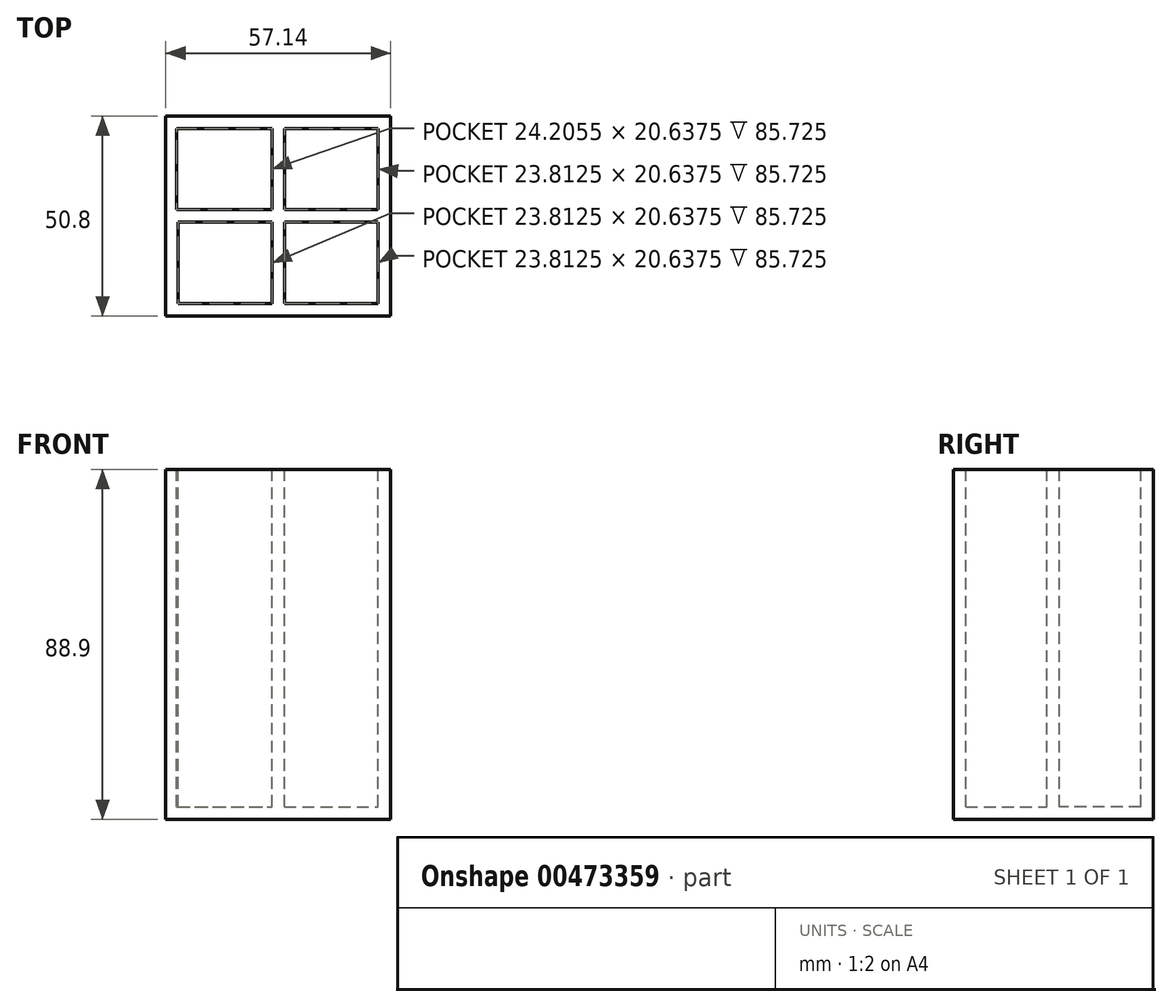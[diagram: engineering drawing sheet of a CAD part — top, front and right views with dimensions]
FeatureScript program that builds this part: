
annotation { "Feature Type Name" : "Feature", "Feature Type Description" : "" }
export const myFeature = defineFeature(function(context is Context, id is Id, definition is map)
    precondition{}
    {
        {
            var Q0;
            Q0=qCreatedBy(makeId("Front.planeOp"),FACE);
            var sketch = newSketch(context, id + "F0", { "sketchPlane" : qUnion([Q0])});
            skLineSegment(sketch, "E0.bottom", {"start": v(-28.57, 44.45) * mm, "end": v(28.58, 44.45) * mm});
            skLineSegment(sketch, "E0.top", {"start": v(-28.58, -44.45) * mm, "end": v(28.58, -44.45) * mm});
            skLineSegment(sketch, "E0.left", {"start": v(-28.57, 44.45) * mm, "end": v(-28.58, -44.45) * mm});
            skLineSegment(sketch, "E0.right", {"start": v(28.58, 44.45) * mm, "end": v(28.58, -44.45) * mm});
            skPoint(sketch, "E0.middle", {"position": v(0, 0) * mm});
            skSolve(sketch);
        }
        {
            var Q0;
            Q0 = qSketchRegion(id + "F0", true);
            extrude(context, id + "F1", {"entities" : qUnion([Q0]), "depth" : 50.8 * mm});
        }
        {
            var Q0;
            Q0=makeQuery(id+"F1.opExtrude","SWEPT_FACE",FACE,{"disambiguationData":[OSD([sQuery(id+"F0.wireOp",EDGE,"E0.bottom")])]});
            var sketch = newSketch(context, id + "F2", { "sketchPlane" : qUnion([Q0])});
            skLineSegment(sketch, "E1.bottom", {"start": v(-25.8, -3.18) * mm, "end": v(-1.59, -3.18) * mm});
            skLineSegment(sketch, "E1.top", {"start": v(-25.8, -23.81) * mm, "end": v(-1.59, -23.81) * mm});
            skLineSegment(sketch, "E1.left", {"start": v(-25.8, -3.18) * mm, "end": v(-25.8, -23.81) * mm});
            skLineSegment(sketch, "E1.right", {"start": v(-1.59, -3.17) * mm, "end": v(-1.59, -23.81) * mm});
            skSolve(sketch);
        }
        {
            var Q0;
            Q0 = qSketchRegion(id + "F2", true);
            extrude(context, id + "F3", {"entities" : qUnion([Q0]), "operationType" : NewBodyOperationType.REMOVE, "oppositeDirection" : true, "depth" : 85.72 * mm});
        }
        {
            var Q0;
            Q0=makeQuery(id+"F1.opExtrude","SWEPT_FACE",FACE,{"disambiguationData":[OSD([sQuery(id+"F0.wireOp",EDGE,"E0.bottom")])]});
            var sketch = newSketch(context, id + "F4", { "sketchPlane" : qUnion([Q0])});
            skLineSegment(sketch, "E2.bottom", {"start": v(-25.8, -3.18) * mm, "end": v(-1.59, -3.18) * mm});
            skLineSegment(sketch, "E2.top", {"start": v(-25.8, -23.81) * mm, "end": v(-1.59, -23.81) * mm});
            skLineSegment(sketch, "E2.left", {"start": v(-25.8, -3.18) * mm, "end": v(-25.8, -23.81) * mm});
            skLineSegment(sketch, "E2.right", {"start": v(-1.59, -3.18) * mm, "end": v(-1.59, -23.81) * mm});
            skLineSegment(sketch, "E3.bottom", {"start": v(1.59, -3.18) * mm, "end": v(25.4, -3.18) * mm});
            skLineSegment(sketch, "E3.top", {"start": v(1.59, -23.81) * mm, "end": v(25.4, -23.81) * mm});
            skLineSegment(sketch, "E3.left", {"start": v(1.59, -3.18) * mm, "end": v(1.59, -23.81) * mm});
            skLineSegment(sketch, "E3.right", {"start": v(25.4, -3.17) * mm, "end": v(25.4, -23.81) * mm});
            skSolve(sketch);
        }
        {
            var Q0;
            Q0=makeQuery(id+"F4.imprint","IMPRINT",FACE,{"disambiguationData":[TD([[makeQuery(id+"F4.imprint","IMPRINT",EDGE,{"derivedFrom":sQuery(id+"F4.wireOp",EDGE,"E3.bottom")}),-1.0]])]});
            extrude(context, id + "F5", {"entities" : qUnion([Q0]), "operationType" : NewBodyOperationType.REMOVE, "oppositeDirection" : true, "depth" : 85.72 * mm});
        }
        {
            var Q0;
            Q0=makeQuery(id+"F1.opExtrude","SWEPT_FACE",FACE,{"disambiguationData":[OSD([sQuery(id+"F0.wireOp",EDGE,"E0.bottom")])]});
            var sketch = newSketch(context, id + "F6", { "sketchPlane" : qUnion([Q0])});
            skLineSegment(sketch, "E4.bottom", {"start": v(-25.4, -47.63) * mm, "end": v(-1.59, -47.63) * mm});
            skLineSegment(sketch, "E4.top", {"start": v(-25.4, -26.99) * mm, "end": v(-1.59, -26.99) * mm});
            skLineSegment(sketch, "E4.left", {"start": v(-25.4, -47.63) * mm, "end": v(-25.4, -26.99) * mm});
            skLineSegment(sketch, "E4.right", {"start": v(-1.59, -47.63) * mm, "end": v(-1.59, -26.99) * mm});
            skSolve(sketch);
        }
        {
            var Q0;
            Q0 = qSketchRegion(id + "F6", true);
            extrude(context, id + "F7", {"entities" : qUnion([Q0]), "operationType" : NewBodyOperationType.REMOVE, "oppositeDirection" : true, "depth" : 85.72 * mm});
        }
        {
            var Q0;
            Q0=makeQuery(id+"F1.opExtrude","SWEPT_FACE",FACE,{"disambiguationData":[OSD([sQuery(id+"F0.wireOp",EDGE,"E0.bottom")])]});
            var sketch = newSketch(context, id + "F8", { "sketchPlane" : qUnion([Q0])});
            skLineSegment(sketch, "E5.bottom", {"start": v(1.59, -26.99) * mm, "end": v(25.4, -26.99) * mm});
            skLineSegment(sketch, "E5.top", {"start": v(1.59, -47.63) * mm, "end": v(25.4, -47.62) * mm});
            skLineSegment(sketch, "E5.left", {"start": v(1.59, -26.99) * mm, "end": v(1.59, -47.63) * mm});
            skLineSegment(sketch, "E5.right", {"start": v(25.4, -26.99) * mm, "end": v(25.4, -47.62) * mm});
            skSolve(sketch);
        }
        {
            var Q0;
            Q0 = qSketchRegion(id + "F8", true);
            extrude(context, id + "F9", {"entities" : qUnion([Q0]), "operationType" : NewBodyOperationType.REMOVE, "oppositeDirection" : true, "depth" : 85.72 * mm});
        }
    });
